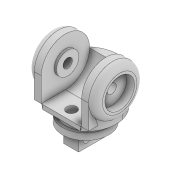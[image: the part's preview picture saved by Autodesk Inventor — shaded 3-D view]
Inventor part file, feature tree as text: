
AUTODESK INVENTOR PART (.ipt)
format: ipt  version: 2020 (Build 240168000, 168)  size: 1,202,688 bytes
history: native  units: mm
features: sketch x16, extrude x15, plane x4, mirror x3, loft x1, fillet x1, projected_geometry x1, other x1
ambient origin geometry x8: Origin, YZ Plane, XZ Plane, XY Plane, X Axis, Y Axis, Z Axis, Center Point
bodies: Solid1 (feature_tree)
feature tree (42):
  extrude  "Extrusion1"  Depth=1.5mm TaperAngle=0.0deg
  extrude  "Extrusion2"  Depth=1.5mm TaperAngle=0.0deg
  extrude  "Extrusion3"  Depth=1.0mm TaperAngle=0.0deg
  extrude  "Extrusion4"  Depth=12.36mm TaperAngle=0.0deg
  extrude  "Extrusion5"  Depth=1.57mm TaperAngle=0.0deg
  extrude  "Extrusion6"  TaperAngle=0.0deg  [1 undecoded]
  mirror  "Mirror1"
  plane  "Work Plane1"
  loft  "Loft1"
  fillet  "Fillet1"  Radius=5.5mm
  plane  "Work Plane3"
  extrude  "Extrusion7"  Depth=11.0mm
  extrude  "Extrusion8"  Depth=5.12mm
  mirror  "Mirror3"
  extrude  "Extrusion9"  Depth=6.75mm
  mirror  "Mirror4"
  extrude  "Extrusion10"  Depth=2.12mm
  extrude  "Extrusion11"  Depth=3.4mm
  extrude  "Extrusion12"  Depth=3.5mm TaperAngle=0.0deg
  extrude  "Extrusion13"  Depth=0.9mm
  plane  "Work Plane4"
  extrude  "Extrusion14"  Depth=0.486mm
  plane  "Work Plane5"
  extrude  "Extrusion15"  Depth=1.8mm
  sketch  "Sketch2"  dims[d0=10.5mm d1=1.5mm d2=0.0mm]
  sketch  "Sketch3"  dims[d3=9.25mm d4=1.5mm d5=0.0mm]
  sketch  "Sketch4"  dims[d6=13.9mm d7=1.0mm d8=0.0mm]
  sketch  "Sketch6"  dims[d9=5.5mm d10=12.36mm d11=0.0mm]
  projected_geometry  "Projected Loop1"
  sketch  "Sketch7"  dims[d12=1.11mm d13=0.0mm d14=1.57mm d15=0.0mm]
  sketch  "Sketch8"  dims[d16=5.5mm d62=0.0mm d63=90.0deg]
  other  "Image1"
  sketch  "Sketch9"  dims[d64=0.0mm d65=90.0deg d66=1.57mm d69=5.5mm]
  sketch  "Sketch11"  dims[d70=5.5mm d71=11.0mm]
  sketch  "Sketch14"  dims[d72=9.2mm d73=0.0mm d81=5.12mm]
  sketch  "Sketch15"  dims[d82=0.5mm d83=0.0mm d84=6.75mm]
  sketch  "Sketch16"  dims[d85=1.8mm d86=0.0mm d87=2.12mm]
  sketch  "Sketch17"  dims[d88=0.0mm d89=0.0mm d90=3.4mm]
  sketch  "Sketch18"  dims[d91=6.6mm d92=3.5mm d93=0.0mm]
  sketch  "Sketch19"  dims[d94=0.486mm d95=0.9mm]
  sketch  "Sketch20"  dims[d96=2.2625mm d97=0.0mm d98=0.486mm]
  sketch  "Sketch21"  dims[d99=0.5625mm d100=1.8mm d101=3.5mm d102=0.0mm d103=27.925268mm d104=2.2mm d105=6.5mm d106=0.0mm d107=3.054326mm d108=2.2mm d109=6.5mm d110=12.5mm d111=0.0mm d112=0.0mm]
note: 1 required parameter value undecoded (feature->parameter linkage not recoverable at this tier; creation-order binding heuristic only, values carry confidence <= 0.55)
